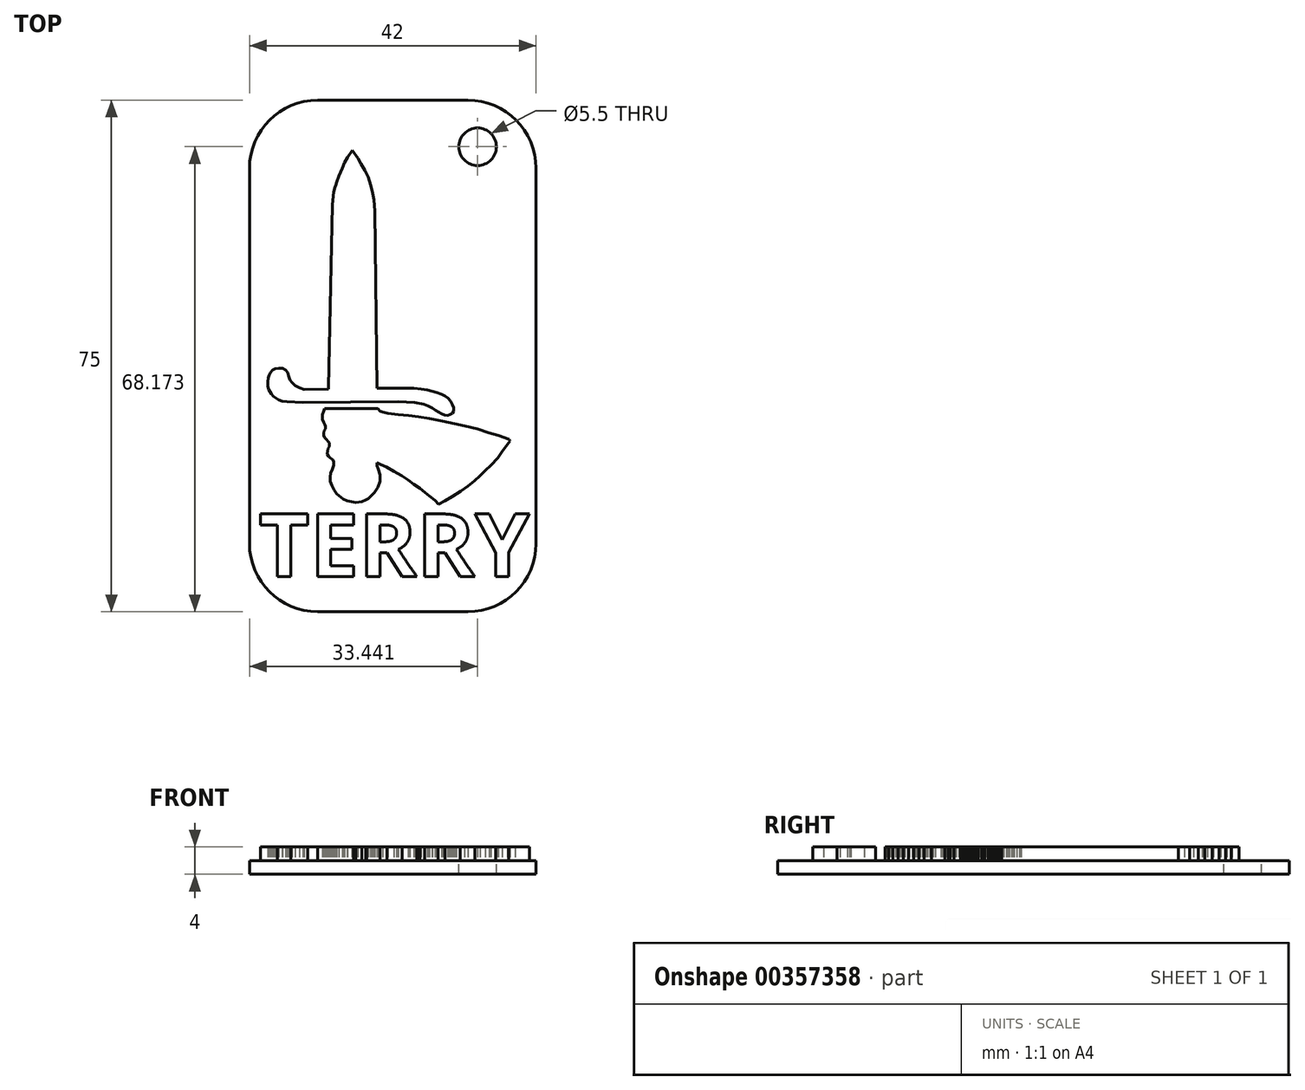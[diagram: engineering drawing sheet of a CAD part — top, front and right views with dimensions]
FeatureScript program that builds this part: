
annotation { "Feature Type Name" : "Feature", "Feature Type Description" : "" }
export const myFeature = defineFeature(function(context is Context, id is Id, definition is map)
    precondition{}
    {
        {
            var Q0;
            Q0=qCreatedBy(makeId("Top.planeOp"),FACE);
            var sketch = newSketch(context, id + "F0", { "sketchPlane" : qUnion([Q0])});
            skLineSegment(sketch, "E0.bottom", {"start": v(-10, 0) * mm, "end": v(-32, 0) * mm});
            skLineSegment(sketch, "E0.top", {"start": v(-10, 75) * mm, "end": v(-32, 75) * mm});
            skLineSegment(sketch, "E0.left", {"start": v(0, 10) * mm, "end": v(0, 65) * mm});
            skLineSegment(sketch, "E0.right", {"start": v(-42, 10) * mm, "end": v(-42, 65) * mm});
            skPoint(sketch, "E1.visualSharp", {"position": v(-42, 75) * mm});
            skArc(sketch, "E1.filletArc", {"start": v(-32, 75) * mm, "mid": v(-39.07, 72.07) * mm, "end": v(-42, 65) * mm});
            skPoint(sketch, "E2.visualSharp", {"position": v(0, 75) * mm});
            skArc(sketch, "E2.filletArc", {"start": v(0, 65) * mm, "mid": v(-2.93, 72.07) * mm, "end": v(-10, 75) * mm});
            skPoint(sketch, "E3.visualSharp", {"position": v(-42, 0) * mm});
            skArc(sketch, "E3.filletArc", {"start": v(-42, 10) * mm, "mid": v(-39.07, 2.93) * mm, "end": v(-32, 0) * mm});
            skPoint(sketch, "E4.visualSharp", {"position": v(0, 0) * mm});
            skArc(sketch, "E4.filletArc", {"start": v(-10, 0) * mm, "mid": v(-2.93, 2.93) * mm, "end": v(0, 10) * mm});
            skSolve(sketch);
        }
        {
            var Q0;
            Q0 = qSketchRegion(id + "F0", true);
            extrude(context, id + "F1", {"entities" : qUnion([Q0]), "depth" : 2 * mm});
        }
        {
            var Q0;
            Q0=makeQuery(id+"F1.opExtrude","CAP_FACE",FACE,{"disambiguationData":[OSD([sQuery(id+"F0.wireOp",EDGE,"E0.bottom"),sQuery(id+"F0.wireOp",EDGE,"E0.top"),sQuery(id+"F0.wireOp",EDGE,"E0.left"),sQuery(id+"F0.wireOp",EDGE,"E0.right"),sQuery(id+"F0.wireOp",EDGE,"E1.filletArc"),sQuery(id+"F0.wireOp",EDGE,"E2.filletArc"),sQuery(id+"F0.wireOp",EDGE,"E3.filletArc"),sQuery(id+"F0.wireOp",EDGE,"E4.filletArc")])],"isStart":false});
            var sketch = newSketch(context, id + "F2", { "sketchPlane" : qUnion([Q0])});
            skLineSegment(sketch, "E5", {"start": v(-24.61, 16.56) * mm, "end": v(-23.69, 17.44) * mm});
            skLineSegment(sketch, "E6", {"start": v(-23.69, 17.44) * mm, "end": v(-23.17, 18.25) * mm});
            skLineSegment(sketch, "E7", {"start": v(-23.17, 18.25) * mm, "end": v(-22.88, 19.12) * mm});
            skLineSegment(sketch, "E8", {"start": v(-22.88, 19.12) * mm, "end": v(-22.88, 20.06) * mm});
            skLineSegment(sketch, "E9", {"start": v(-22.88, 20.06) * mm, "end": v(-23.15, 20.87) * mm});
            skLineSegment(sketch, "E10", {"start": v(-23.15, 20.87) * mm, "end": v(-23.28, 21.41) * mm});
            skLineSegment(sketch, "E11", {"start": v(-23.28, 21.41) * mm, "end": v(-23.28, 21.82) * mm});
            skLineSegment(sketch, "E12", {"start": v(-23.28, 21.82) * mm, "end": v(-22.8, 21.6) * mm});
            skLineSegment(sketch, "E13", {"start": v(-22.8, 21.6) * mm, "end": v(-21.9, 21.21) * mm});
            skLineSegment(sketch, "E14", {"start": v(-21.9, 21.21) * mm, "end": v(-20.84, 20.58) * mm});
            skLineSegment(sketch, "E15", {"start": v(-20.84, 20.58) * mm, "end": v(-19.7, 19.91) * mm});
            skLineSegment(sketch, "E16", {"start": v(-19.7, 19.91) * mm, "end": v(-18.72, 19.3) * mm});
            skLineSegment(sketch, "E17", {"start": v(-18.72, 19.3) * mm, "end": v(-17.9, 18.7) * mm});
            skLineSegment(sketch, "E18", {"start": v(-17.9, 18.7) * mm, "end": v(-17.02, 18.08) * mm});
            skLineSegment(sketch, "E19", {"start": v(-17.02, 18.08) * mm, "end": v(-16.24, 17.46) * mm});
            skLineSegment(sketch, "E20", {"start": v(-16.24, 17.46) * mm, "end": v(-15.6, 16.98) * mm});
            skLineSegment(sketch, "E21", {"start": v(-15.6, 16.98) * mm, "end": v(-14.8, 16.3) * mm});
            skLineSegment(sketch, "E22", {"start": v(-14.8, 16.3) * mm, "end": v(-14.27, 15.76) * mm});
            skLineSegment(sketch, "E23", {"start": v(-14.27, 15.76) * mm, "end": v(-13.32, 16.25) * mm});
            skLineSegment(sketch, "E24", {"start": v(-13.32, 16.25) * mm, "end": v(-12.27, 16.87) * mm});
            skLineSegment(sketch, "E25", {"start": v(-12.27, 16.87) * mm, "end": v(-11.07, 17.67) * mm});
            skLineSegment(sketch, "E26", {"start": v(-11.07, 17.67) * mm, "end": v(-9.97, 18.44) * mm});
            skLineSegment(sketch, "E27", {"start": v(-9.97, 18.44) * mm, "end": v(-9.01, 19.2) * mm});
            skLineSegment(sketch, "E28", {"start": v(-9.01, 19.2) * mm, "end": v(-8.2, 19.94) * mm});
            skLineSegment(sketch, "E29", {"start": v(-8.2, 19.94) * mm, "end": v(-7.41, 20.7) * mm});
            skLineSegment(sketch, "E30", {"start": v(-7.41, 20.7) * mm, "end": v(-6.61, 21.49) * mm});
            skLineSegment(sketch, "E31", {"start": v(-6.61, 21.49) * mm, "end": v(-5.61, 22.54) * mm});
            skLineSegment(sketch, "E32", {"start": v(-5.61, 22.54) * mm, "end": v(-4.94, 23.49) * mm});
            skLineSegment(sketch, "E33", {"start": v(-4.94, 23.49) * mm, "end": v(-4.22, 24.52) * mm});
            skLineSegment(sketch, "E34", {"start": v(-4.22, 24.52) * mm, "end": v(-3.83, 25) * mm});
            skLineSegment(sketch, "E35", {"start": v(-3.83, 25) * mm, "end": v(-3.94, 25.3) * mm});
            skLineSegment(sketch, "E36", {"start": v(-3.94, 25.3) * mm, "end": v(-5.5, 25.84) * mm});
            skLineSegment(sketch, "E37", {"start": v(-5.5, 25.84) * mm, "end": v(-6.9, 26.25) * mm});
            skLineSegment(sketch, "E38", {"start": v(-6.9, 26.25) * mm, "end": v(-8.6, 26.78) * mm});
            skLineSegment(sketch, "E39", {"start": v(-8.6, 26.78) * mm, "end": v(-10.46, 27.22) * mm});
            skLineSegment(sketch, "E40", {"start": v(-10.46, 27.22) * mm, "end": v(-11.92, 27.6) * mm});
            skLineSegment(sketch, "E41", {"start": v(-11.92, 27.6) * mm, "end": v(-13.7, 27.96) * mm});
            skLineSegment(sketch, "E42", {"start": v(-13.7, 27.96) * mm, "end": v(-15.6, 28.33) * mm});
            skLineSegment(sketch, "E43", {"start": v(-15.6, 28.33) * mm, "end": v(-17.18, 28.59) * mm});
            skLineSegment(sketch, "E44", {"start": v(-17.18, 28.59) * mm, "end": v(-18.7, 28.75) * mm});
            skLineSegment(sketch, "E45", {"start": v(-18.7, 28.75) * mm, "end": v(-20.2, 28.88) * mm});
            skLineSegment(sketch, "E46", {"start": v(-20.2, 28.88) * mm, "end": v(-21.74, 29.08) * mm});
            skLineSegment(sketch, "E47", {"start": v(-21.74, 29.08) * mm, "end": v(-22.5, 29.26) * mm});
            skLineSegment(sketch, "E48", {"start": v(-22.5, 29.26) * mm, "end": v(-22.87, 29.41) * mm});
            skLineSegment(sketch, "E49", {"start": v(-22.87, 29.41) * mm, "end": v(-23.2, 29.78) * mm});
            skLineSegment(sketch, "E50", {"start": v(-23.2, 29.78) * mm, "end": v(-31, 29.78) * mm});
            skLineSegment(sketch, "E51", {"start": v(-31, 29.78) * mm, "end": v(-31.14, 29.39) * mm});
            skLineSegment(sketch, "E52", {"start": v(-31.14, 29.39) * mm, "end": v(-31.3, 28.87) * mm});
            skLineSegment(sketch, "E53", {"start": v(-31.3, 28.87) * mm, "end": v(-31.3, 28.55) * mm});
            skLineSegment(sketch, "E54", {"start": v(-31.3, 28.55) * mm, "end": v(-31.3, 28.19) * mm});
            skLineSegment(sketch, "E55", {"start": v(-31.3, 28.19) * mm, "end": v(-31.1, 27.76) * mm});
            skLineSegment(sketch, "E56", {"start": v(-31.1, 27.76) * mm, "end": v(-30.93, 27.36) * mm});
            skLineSegment(sketch, "E57", {"start": v(-30.93, 27.36) * mm, "end": v(-30.86, 27.15) * mm});
            skLineSegment(sketch, "E58", {"start": v(-30.86, 27.15) * mm, "end": v(-30.86, 26.83) * mm});
            skLineSegment(sketch, "E59", {"start": v(-30.86, 26.83) * mm, "end": v(-31.06, 26.58) * mm});
            skLineSegment(sketch, "E60", {"start": v(-31.06, 26.58) * mm, "end": v(-31.13, 26.18) * mm});
            skLineSegment(sketch, "E61", {"start": v(-31.13, 26.18) * mm, "end": v(-31.13, 25.82) * mm});
            skLineSegment(sketch, "E62", {"start": v(-31.13, 25.82) * mm, "end": v(-31, 25.51) * mm});
            skLineSegment(sketch, "E63", {"start": v(-31, 25.51) * mm, "end": v(-30.7, 25.2) * mm});
            skLineSegment(sketch, "E64", {"start": v(-30.7, 25.2) * mm, "end": v(-30.46, 24.94) * mm});
            skLineSegment(sketch, "E65", {"start": v(-30.46, 24.94) * mm, "end": v(-30.31, 24.76) * mm});
            skLineSegment(sketch, "E66", {"start": v(-30.31, 24.76) * mm, "end": v(-30.31, 24.52) * mm});
            skLineSegment(sketch, "E67", {"start": v(-30.31, 24.52) * mm, "end": v(-30.27, 24.22) * mm});
            skLineSegment(sketch, "E68", {"start": v(-30.27, 24.22) * mm, "end": v(-30.48, 23.96) * mm});
            skLineSegment(sketch, "E69", {"start": v(-30.48, 23.96) * mm, "end": v(-30.54, 23.58) * mm});
            skLineSegment(sketch, "E70", {"start": v(-30.54, 23.58) * mm, "end": v(-30.62, 23.14) * mm});
            skLineSegment(sketch, "E71", {"start": v(-30.62, 23.14) * mm, "end": v(-30.44, 22.8) * mm});
            skLineSegment(sketch, "E72", {"start": v(-30.44, 22.8) * mm, "end": v(-30.14, 22.53) * mm});
            skLineSegment(sketch, "E73", {"start": v(-30.14, 22.53) * mm, "end": v(-29.8, 22.3) * mm});
            skLineSegment(sketch, "E74", {"start": v(-29.8, 22.3) * mm, "end": v(-29.68, 21.98) * mm});
            skLineSegment(sketch, "E75", {"start": v(-29.68, 21.98) * mm, "end": v(-29.68, 21.47) * mm});
            skLineSegment(sketch, "E76", {"start": v(-29.68, 21.47) * mm, "end": v(-29.87, 20.87) * mm});
            skLineSegment(sketch, "E77", {"start": v(-29.87, 20.87) * mm, "end": v(-30.09, 20.3) * mm});
            skLineSegment(sketch, "E78", {"start": v(-30.09, 20.3) * mm, "end": v(-30.18, 19.76) * mm});
            skLineSegment(sketch, "E79", {"start": v(-30.18, 19.76) * mm, "end": v(-30.18, 19.11) * mm});
            skLineSegment(sketch, "E80", {"start": v(-30.18, 19.11) * mm, "end": v(-29.94, 18.5) * mm});
            skLineSegment(sketch, "E81", {"start": v(-29.94, 18.5) * mm, "end": v(-29.6, 17.88) * mm});
            skLineSegment(sketch, "E82", {"start": v(-29.6, 17.88) * mm, "end": v(-29.22, 17.26) * mm});
            skLineSegment(sketch, "E83", {"start": v(-29.22, 17.26) * mm, "end": v(-28.72, 16.86) * mm});
            skLineSegment(sketch, "E84", {"start": v(-28.72, 16.86) * mm, "end": v(-28.25, 16.49) * mm});
            skLineSegment(sketch, "E85", {"start": v(-28.25, 16.49) * mm, "end": v(-27.7, 16.25) * mm});
            skLineSegment(sketch, "E86", {"start": v(-27.7, 16.25) * mm, "end": v(-27.09, 16.14) * mm});
            skLineSegment(sketch, "E87", {"start": v(-27.09, 16.14) * mm, "end": v(-26.44, 16.03) * mm});
            skLineSegment(sketch, "E88", {"start": v(-26.44, 16.03) * mm, "end": v(-25.56, 16.14) * mm});
            skLineSegment(sketch, "E89", {"start": v(-25.56, 16.14) * mm, "end": v(-24.97, 16.38) * mm});
            skLineSegment(sketch, "E90", {"start": v(-24.97, 16.38) * mm, "end": v(-24.61, 16.56) * mm});
            skLineSegment(sketch, "E91", {"start": v(-23.28, 32.85) * mm, "end": v(-23.62, 58.76) * mm});
            skLineSegment(sketch, "E92", {"start": v(-23.62, 58.76) * mm, "end": v(-23.73, 60.41) * mm});
            skLineSegment(sketch, "E93", {"start": v(-23.73, 60.41) * mm, "end": v(-24, 61.68) * mm});
            skLineSegment(sketch, "E94", {"start": v(-24, 61.68) * mm, "end": v(-24.27, 62.63) * mm});
            skLineSegment(sketch, "E95", {"start": v(-24.27, 62.63) * mm, "end": v(-24.61, 63.72) * mm});
            skLineSegment(sketch, "E96", {"start": v(-24.61, 63.72) * mm, "end": v(-25.1, 64.73) * mm});
            skLineSegment(sketch, "E97", {"start": v(-25.1, 64.73) * mm, "end": v(-25.64, 65.7) * mm});
            skLineSegment(sketch, "E98", {"start": v(-25.64, 65.7) * mm, "end": v(-26.14, 66.47) * mm});
            skLineSegment(sketch, "E99", {"start": v(-26.14, 66.47) * mm, "end": v(-26.93, 67.62) * mm});
            skLineSegment(sketch, "E100", {"start": v(-26.93, 67.62) * mm, "end": v(-27.62, 66.62) * mm});
            skLineSegment(sketch, "E101", {"start": v(-27.62, 66.62) * mm, "end": v(-28.04, 65.85) * mm});
            skLineSegment(sketch, "E102", {"start": v(-28.04, 65.85) * mm, "end": v(-28.41, 65) * mm});
            skLineSegment(sketch, "E103", {"start": v(-28.41, 65) * mm, "end": v(-28.92, 63.9) * mm});
            skLineSegment(sketch, "E104", {"start": v(-28.92, 63.9) * mm, "end": v(-29.2, 63.02) * mm});
            skLineSegment(sketch, "E105", {"start": v(-29.2, 63.02) * mm, "end": v(-29.38, 62.52) * mm});
            skLineSegment(sketch, "E106", {"start": v(-29.38, 62.52) * mm, "end": v(-29.47, 62.22) * mm});
            skLineSegment(sketch, "E107", {"start": v(-29.47, 62.22) * mm, "end": v(-29.63, 61.54) * mm});
            skLineSegment(sketch, "E108", {"start": v(-29.63, 61.54) * mm, "end": v(-29.74, 60.94) * mm});
            skLineSegment(sketch, "E109", {"start": v(-29.74, 60.94) * mm, "end": v(-29.85, 59.62) * mm});
            skLineSegment(sketch, "E110", {"start": v(-29.85, 59.62) * mm, "end": v(-30.44, 32.88) * mm});
            skLineSegment(sketch, "E111", {"start": v(-30.44, 32.88) * mm, "end": v(-30.44, 32.63) * mm});
            skLineSegment(sketch, "E112", {"start": v(-30.44, 32.63) * mm, "end": v(-33.98, 32.58) * mm});
            skLineSegment(sketch, "E113", {"start": v(-33.98, 32.58) * mm, "end": v(-34.7, 32.81) * mm});
            skLineSegment(sketch, "E114", {"start": v(-34.7, 32.81) * mm, "end": v(-35.3, 33.16) * mm});
            skLineSegment(sketch, "E115", {"start": v(-35.3, 33.16) * mm, "end": v(-35.73, 33.57) * mm});
            skLineSegment(sketch, "E116", {"start": v(-35.73, 33.57) * mm, "end": v(-36.04, 34) * mm});
            skLineSegment(sketch, "E117", {"start": v(-36.04, 34) * mm, "end": v(-36.25, 34.52) * mm});
            skLineSegment(sketch, "E118", {"start": v(-36.25, 34.52) * mm, "end": v(-36.42, 35.05) * mm});
            skLineSegment(sketch, "E119", {"start": v(-36.42, 35.05) * mm, "end": v(-36.71, 35.42) * mm});
            skLineSegment(sketch, "E120", {"start": v(-36.71, 35.42) * mm, "end": v(-37.14, 35.67) * mm});
            skLineSegment(sketch, "E121", {"start": v(-37.14, 35.67) * mm, "end": v(-37.73, 35.72) * mm});
            skLineSegment(sketch, "E122", {"start": v(-37.73, 35.72) * mm, "end": v(-38.26, 35.65) * mm});
            skLineSegment(sketch, "E123", {"start": v(-38.26, 35.65) * mm, "end": v(-38.61, 35.42) * mm});
            skLineSegment(sketch, "E124", {"start": v(-38.61, 35.42) * mm, "end": v(-38.9, 35.05) * mm});
            skLineSegment(sketch, "E125", {"start": v(-38.9, 35.05) * mm, "end": v(-39.11, 34.7) * mm});
            skLineSegment(sketch, "E126", {"start": v(-39.11, 34.7) * mm, "end": v(-39.24, 34.3) * mm});
            skLineSegment(sketch, "E127", {"start": v(-39.24, 34.3) * mm, "end": v(-39.3, 33.74) * mm});
            skLineSegment(sketch, "E128", {"start": v(-39.3, 33.74) * mm, "end": v(-39.29, 33.02) * mm});
            skLineSegment(sketch, "E129", {"start": v(-39.29, 33.02) * mm, "end": v(-39.2, 32.6) * mm});
            skLineSegment(sketch, "E130", {"start": v(-39.2, 32.6) * mm, "end": v(-39, 32.27) * mm});
            skLineSegment(sketch, "E131", {"start": v(-39, 32.27) * mm, "end": v(-38.78, 31.94) * mm});
            skLineSegment(sketch, "E132", {"start": v(-38.78, 31.94) * mm, "end": v(-38.47, 31.58) * mm});
            skLineSegment(sketch, "E133", {"start": v(-38.47, 31.58) * mm, "end": v(-38.13, 31.3) * mm});
            skLineSegment(sketch, "E134", {"start": v(-38.13, 31.3) * mm, "end": v(-37.7, 31.06) * mm});
            skLineSegment(sketch, "E135", {"start": v(-37.7, 31.06) * mm, "end": v(-37.25, 30.89) * mm});
            skLineSegment(sketch, "E136", {"start": v(-37.25, 30.89) * mm, "end": v(-36.51, 30.78) * mm});
            skLineSegment(sketch, "E137", {"start": v(-36.51, 30.78) * mm, "end": v(-35.6, 30.73) * mm});
            skLineSegment(sketch, "E138", {"start": v(-35.6, 30.73) * mm, "end": v(-34.14, 30.65) * mm});
            skLineSegment(sketch, "E139", {"start": v(-34.14, 30.65) * mm, "end": v(-20.22, 30.78) * mm});
            skLineSegment(sketch, "E140", {"start": v(-20.22, 30.78) * mm, "end": v(-17.78, 30.65) * mm});
            skLineSegment(sketch, "E141", {"start": v(-17.78, 30.65) * mm, "end": v(-16.44, 30.4) * mm});
            skLineSegment(sketch, "E142", {"start": v(-16.44, 30.4) * mm, "end": v(-15.84, 30.17) * mm});
            skLineSegment(sketch, "E143", {"start": v(-15.84, 30.17) * mm, "end": v(-15.21, 29.87) * mm});
            skLineSegment(sketch, "E144", {"start": v(-15.21, 29.87) * mm, "end": v(-14.7, 29.52) * mm});
            skLineSegment(sketch, "E145", {"start": v(-14.7, 29.52) * mm, "end": v(-14.3, 29.26) * mm});
            skLineSegment(sketch, "E146", {"start": v(-14.3, 29.26) * mm, "end": v(-13.85, 29.02) * mm});
            skLineSegment(sketch, "E147", {"start": v(-13.85, 29.02) * mm, "end": v(-13.41, 28.85) * mm});
            skLineSegment(sketch, "E148", {"start": v(-13.41, 28.85) * mm, "end": v(-12.98, 28.79) * mm});
            skLineSegment(sketch, "E149", {"start": v(-12.98, 28.79) * mm, "end": v(-12.62, 28.9) * mm});
            skLineSegment(sketch, "E150", {"start": v(-12.62, 28.9) * mm, "end": v(-12.3, 29.12) * mm});
            skLineSegment(sketch, "E151", {"start": v(-12.3, 29.12) * mm, "end": v(-12.1, 29.39) * mm});
            skLineSegment(sketch, "E152", {"start": v(-12.1, 29.39) * mm, "end": v(-12.07, 29.94) * mm});
            skLineSegment(sketch, "E153", {"start": v(-12.07, 29.94) * mm, "end": v(-12.24, 30.37) * mm});
            skLineSegment(sketch, "E154", {"start": v(-12.24, 30.37) * mm, "end": v(-12.53, 30.89) * mm});
            skLineSegment(sketch, "E155", {"start": v(-12.53, 30.89) * mm, "end": v(-12.93, 31.33) * mm});
            skLineSegment(sketch, "E156", {"start": v(-12.93, 31.33) * mm, "end": v(-13.33, 31.63) * mm});
            skLineSegment(sketch, "E157", {"start": v(-13.33, 31.63) * mm, "end": v(-13.85, 31.87) * mm});
            skLineSegment(sketch, "E158", {"start": v(-13.85, 31.87) * mm, "end": v(-14.57, 32.15) * mm});
            skLineSegment(sketch, "E159", {"start": v(-14.57, 32.15) * mm, "end": v(-15.22, 32.34) * mm});
            skLineSegment(sketch, "E160", {"start": v(-15.22, 32.34) * mm, "end": v(-15.95, 32.54) * mm});
            skLineSegment(sketch, "E161", {"start": v(-15.95, 32.54) * mm, "end": v(-16.8, 32.62) * mm});
            skLineSegment(sketch, "E162", {"start": v(-16.8, 32.62) * mm, "end": v(-17.93, 32.74) * mm});
            skLineSegment(sketch, "E163", {"start": v(-17.93, 32.74) * mm, "end": v(-23.28, 32.74) * mm});
            skLineSegment(sketch, "E164", {"start": v(-23.28, 32.74) * mm, "end": v(-23.28, 32.85) * mm});
            skSolve(sketch);
        }
        {
            var Q0;
            Q0=makeQuery(id+"F2.imprint","IMPRINT",FACE,{"disambiguationData":[TD([[makeQuery(id+"F2.imprint","IMPRINT",EDGE,{"derivedFrom":sQuery(id+"F2.wireOp",EDGE,"E5")}),1.0]])]});
            var Q1;
            Q1=makeQuery(id+"F2.imprint","IMPRINT",FACE,{"disambiguationData":[TD([[makeQuery(id+"F2.imprint","IMPRINT",EDGE,{"derivedFrom":sQuery(id+"F2.wireOp",EDGE,"E91")}),1.0]])]});
            extrude(context, id + "F3", {"entities" : qUnion([Q0, Q1]), "operationType" : NewBodyOperationType.ADD, "depth" : 2 * mm});
        }
        {
            var Q0;
            Q0=makeQuery(id+"F1.opExtrude","CAP_FACE",FACE,{"disambiguationData":[OSD([sQuery(id+"F0.wireOp",EDGE,"E0.bottom"),sQuery(id+"F0.wireOp",EDGE,"E0.top"),sQuery(id+"F0.wireOp",EDGE,"E0.left"),sQuery(id+"F0.wireOp",EDGE,"E0.right"),sQuery(id+"F0.wireOp",EDGE,"E1.filletArc"),sQuery(id+"F0.wireOp",EDGE,"E2.filletArc"),sQuery(id+"F0.wireOp",EDGE,"E3.filletArc"),sQuery(id+"F0.wireOp",EDGE,"E4.filletArc")])],"isStart":false});
            var sketch = newSketch(context, id + "F4", { "sketchPlane" : qUnion([Q0])});
            skText(sketch, "E165", { "text": "TERRY", "fontName": "OpenSans-Bold.ttf"});
            const initialGuessF4  = {"E165": [-0.04064, 0.00514, 1, 0, 0.00927]};
            skSetInitialGuess(sketch, initialGuessF4);
            skSolve(sketch);
        }
        {
            var Q0;
            Q0 = qSketchRegion(id + "F4", true);
            extrude(context, id + "F5", {"entities" : qUnion([Q0]), "operationType" : NewBodyOperationType.ADD, "depth" : 2 * mm});
        }
        {
            var Q0;
            {var subQ0=sQuery(id+"F0.wireOp",EDGE,"E0.left");var subQ1=sQuery(id+"F0.wireOp",EDGE,"E4.filletArc");var subQ2=sQuery(id+"F0.wireOp",EDGE,"E3.filletArc");var subQ3=sQuery(id+"F0.wireOp",EDGE,"E2.filletArc");var subQ4=sQuery(id+"F0.wireOp",EDGE,"E1.filletArc");var subQ5=sQuery(id+"F0.wireOp",EDGE,"E0.bottom");var subQ6=sQuery(id+"F0.wireOp",EDGE,"E0.right");var subQ7=sQuery(id+"F0.wireOp",EDGE,"E0.top");Q0=makeQuery(id+"F5.boolean.opBoolean","SPLIT",FACE,{"disambiguationData":[TD([makeQuery(id+"F1.opExtrude","SWEPT_FACE",FACE,{"disambiguationData":[OSD([subQ5])]})])],"derivedFrom":makeQuery(id+"F1.opExtrude","CAP_FACE",FACE,{"disambiguationData":[OSD([subQ5,subQ7,subQ0,subQ6,subQ4,subQ3,subQ2,subQ1])],"isStart":false})});}
            var sketch = newSketch(context, id + "F6", { "sketchPlane" : qUnion([Q0])});
            skCircle(sketch, "E166", {"center": v(-8.56, 68.17) * mm, "radius": 2.75 * mm});
            skSolve(sketch);
        }
        {
            var Q0;
            Q0=makeQuery(id+"F6.imprint","IMPRINT",FACE,{"disambiguationData":[TD([[makeQuery(id+"F6.imprint","IMPRINT",EDGE,{"derivedFrom":sQuery(id+"F6.wireOp",EDGE,"E166")}),1.0]])]});
            extrude(context, id + "F7", {"entities" : qUnion([Q0]), "operationType" : NewBodyOperationType.REMOVE, "oppositeDirection" : true, "depth" : 25 * mm});
        }
    });
